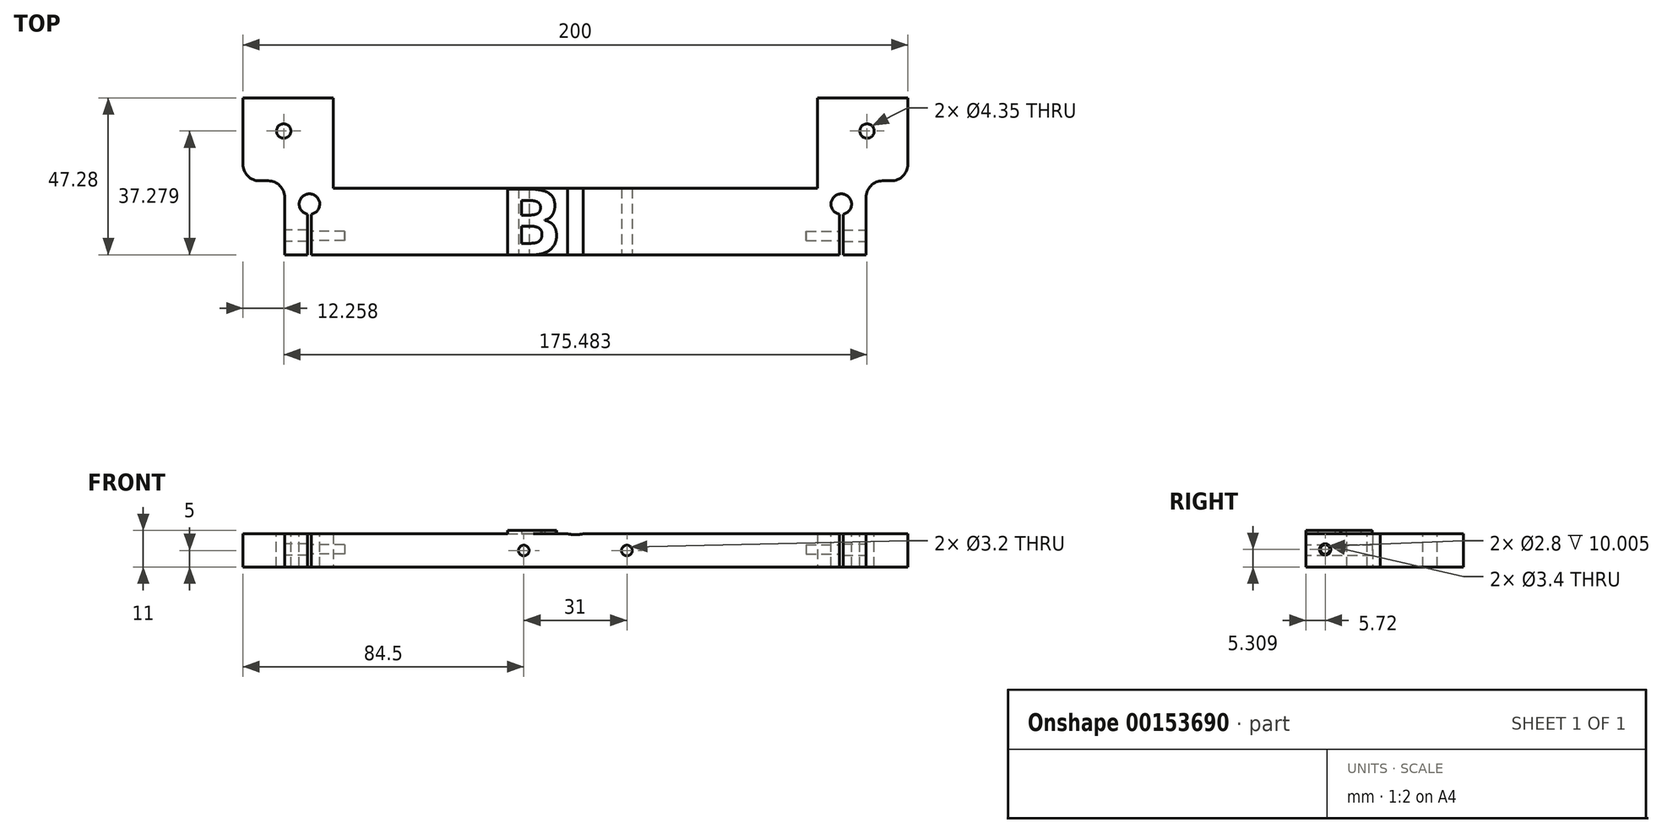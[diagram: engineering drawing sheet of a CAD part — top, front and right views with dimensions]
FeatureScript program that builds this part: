
annotation { "Feature Type Name" : "Feature", "Feature Type Description" : "" }
export const myFeature = defineFeature(function(context is Context, id is Id, definition is map)
    precondition{}
    {
        {
            var Q0;
            Q0=qCreatedBy(makeId("Top.planeOp"),FACE);
            var sketch = newSketch(context, id + "F0", { "sketchPlane" : qUnion([Q0])});
            skLineSegment(sketch, "E0", {"start": v(0, -13.82) * mm, "end": v(-87.44, -13.82) * mm});
            skLineSegment(sketch, "E1", {"start": v(-87.44, -13.82) * mm, "end": v(-87.44, 8.46) * mm});
            skLineSegment(sketch, "E2", {"start": v(-87.44, 8.46) * mm, "end": v(-100, 8.46) * mm});
            skLineSegment(sketch, "E3", {"start": v(-100, 8.46) * mm, "end": v(-100, 33.46) * mm});
            skLineSegment(sketch, "E4", {"start": v(-100, 33.46) * mm, "end": v(-72.87, 33.46) * mm});
            skLineSegment(sketch, "E5", {"start": v(-72.87, 33.46) * mm, "end": v(-72.87, 6.18) * mm});
            skLineSegment(sketch, "E6", {"start": v(-72.87, 6.18) * mm, "end": v(0, 6.18) * mm});
            skLineSegment(sketch, "E7", {"start": v(0, 6.18) * mm, "end": v(0, -13.82) * mm});
            skSolve(sketch);
        }
        {
            var Q0;
            Q0=qSketchRegion(id+"F0",true);
            extrude(context, id + "F1", {"entities" : qUnion([Q0]), "depth" : 10 * mm});
        }
        {
            var Q0;
            Q0=makeQuery(id+"F1.opExtrude","SWEPT_FACE",FACE,{"disambiguationData":[OSD([sQuery(id+"F0.wireOp",EDGE,"E0")])]});
            var sketch = newSketch(context, id + "F2", { "sketchPlane" : qUnion([Q0])});
            skLineSegment(sketch, "E8", {"start": v(0, 5) * mm, "end": v(0, 5) * mm});
            skCircle(sketch, "E9", {"center": v(-15.5, 5) * mm, "radius": 1.6 * mm});
            skCircle(sketch, "E10", {"center": v(0, 20.5) * mm, "radius": 10.75 * mm});
            skSolve(sketch);
        }
        {
            var Q0;
            Q0=qSketchRegion(id+"F2",true);
            extrude(context, id + "F3", {"entities" : qUnion([Q0]), "operationType" : NewBodyOperationType.REMOVE, "endBound" : BoundingType.THROUGH_ALL, "oppositeDirection" : true, "depth" : 25 * mm});
        }
        {
            var Q0;
            {var subQ0=makeQuery(id+"F1.opExtrude","CAP_FACE",FACE,{"disambiguationData":[OSD([sQuery(id+"F0.wireOp",EDGE,"E0"),sQuery(id+"F0.wireOp",EDGE,"fd64a43a-5635-4f94-a977-4dd36923accb"),sQuery(id+"F0.wireOp",EDGE,"1334f7d4-4c90-4769-8fa3-fe5f576fb005"),sQuery(id+"F0.wireOp",EDGE,"E1"),sQuery(id+"F0.wireOp",EDGE,"E2"),sQuery(id+"F0.wireOp",EDGE,"E3"),sQuery(id+"F0.wireOp",EDGE,"E4"),sQuery(id+"F0.wireOp",EDGE,"E5"),sQuery(id+"F0.wireOp",EDGE,"E6"),sQuery(id+"F0.wireOp",EDGE,"E7")])],"isStart":false});Q0=makeQuery(id+"F11.boolean.opBoolean","MERGE",FACE,{"derivedFrom":[subQ0,makeQuery(id+"F11.opPattern","COPY",FACE,{"derivedFrom":subQ0,"instanceName":"1"})]});}
            var sketch = newSketch(context, id + "F4", { "sketchPlane" : qUnion([Q0])});
            skCircle(sketch, "E11", {"center": v(-80, 1.46) * mm, "radius": 3.1 * mm});
            skCircle(sketch, "E12", {"center": v(-87.74, 23.46) * mm, "radius": 2.17 * mm});
            skLineSegment(sketch, "E13", {"start": v(-80, 1.46) * mm, "end": v(-80, -13.82) * mm, "construction": true});
            skLineSegment(sketch, "E14.bottom", {"start": v(-80.55, -0.71) * mm, "end": v(-79.45, -0.71) * mm});
            skLineSegment(sketch, "E14.top", {"start": v(-80.55, -13.82) * mm, "end": v(-79.45, -13.82) * mm});
            skLineSegment(sketch, "E14.left", {"start": v(-80.55, -0.71) * mm, "end": v(-80.55, -13.82) * mm});
            skLineSegment(sketch, "E14.right", {"start": v(-79.45, -0.71) * mm, "end": v(-79.45, -13.82) * mm});
            skPoint(sketch, "E15", {"position": v(-80, -0.71) * mm});
            skSolve(sketch);
        }
        {
            var Q0;
            Q0=qSketchRegion(id+"F4",true);
            var Q1;
            {var subQ3=sQuery(id+"F4.wireOp",EDGE,"E14.bottom");Q1=makeQuery(id+"F4.imprint","IMPRINT",FACE,{"disambiguationData":[TD([[makeQuery(id+"F4.imprint","IMPRINT",EDGE,{"derivedFrom":subQ3}),-1.0]])]});}
            extrude(context, id + "F5", {"entities" : qUnion([Q0, Q1]), "operationType" : NewBodyOperationType.REMOVE, "endBound" : BoundingType.THROUGH_ALL, "oppositeDirection" : true, "depth" : 25 * mm});
        }
        {
            var Q0;
            Q0=makeQuery(id+"F1.opExtrude","SWEPT_EDGE",EDGE,{"disambiguationData":[OSD([sQuery(id+"F0.wireOp",EDGE,"E2"),sQuery(id+"F0.wireOp",EDGE,"E3")])]});
            fillet(context, id + "F6", {"entities" : qUnion([Q0]), "radius" : 5 * mm, "tangentPropagation" : true, "allowEdgeOverflow" : false});
        }
        {
            var Q0;
            Q0=makeQuery(id+"F1.opExtrude","SWEPT_EDGE",EDGE,{"disambiguationData":[OSD([sQuery(id+"F0.wireOp",EDGE,"E1"),sQuery(id+"F0.wireOp",EDGE,"E2")])]});
            fillet(context, id + "F7", {"entities" : qUnion([Q0]), "radius" : 5 * mm, "tangentPropagation" : true, "allowEdgeOverflow" : false});
        }
        {
            var Q0;
            Q0=makeQuery(id+"F1.opExtrude","SWEPT_FACE",FACE,{"disambiguationData":[OSD([sQuery(id+"F0.wireOp",EDGE,"E1")])]});
            var sketch = newSketch(context, id + "F8", { "sketchPlane" : qUnion([Q0])});
            skCircle(sketch, "E16", {"center": v(8.1, 5.3) * mm, "radius": 1.7 * mm});
            skCircle(sketch, "E17", {"center": v(8.1, 5.3) * mm, "radius": 1.4 * mm});
            skSolve(sketch);
        }
        {
            var Q0;
            Q0=makeQuery(id+"F8.imprint","IMPRINT",FACE,{"disambiguationData":[TD([[makeQuery(id+"F8.imprint","IMPRINT",EDGE,{"derivedFrom":sQuery(id+"F8.wireOp",EDGE,"E17")}),1.0]])]});
            extrude(context, id + "F9", {"entities" : qUnion([Q0]), "operationType" : NewBodyOperationType.REMOVE, "oppositeDirection" : true, "depth" : 18 * mm});
        }
        {
            var Q0;
            Q0=makeQuery(id+"F8.imprint","IMPRINT",FACE,{"disambiguationData":[TD([[makeQuery(id+"F8.imprint","IMPRINT",EDGE,{"derivedFrom":sQuery(id+"F8.wireOp",EDGE,"E17")}),1.0]])]});
            var Q1;
            Q1=makeQuery(id+"F8.imprint","IMPRINT",FACE,{"disambiguationData":[TD([[makeQuery(id+"F8.imprint","IMPRINT",EDGE,{"derivedFrom":sQuery(id+"F8.wireOp",EDGE,"E16")}),1.0]])]});
            extrude(context, id + "F10", {"entities" : qUnion([Q0, Q1]), "operationType" : NewBodyOperationType.REMOVE, "endBound" : BoundingType.UP_TO_NEXT, "oppositeDirection" : true, "depth" : 25 * mm});
        }
        {
            var Q0;
            Q0=makeQuery(id+"F1.opExtrude","SWEPT_BODY",BODY,{"disambiguationData":[OSD([sQuery(id+"F0.wireOp",EDGE,"E0"),sQuery(id+"F0.wireOp",EDGE,"fd64a43a-5635-4f94-a977-4dd36923accb"),sQuery(id+"F0.wireOp",EDGE,"1334f7d4-4c90-4769-8fa3-fe5f576fb005"),sQuery(id+"F0.wireOp",EDGE,"E1"),sQuery(id+"F0.wireOp",EDGE,"E2"),sQuery(id+"F0.wireOp",EDGE,"E3"),sQuery(id+"F0.wireOp",EDGE,"E4"),sQuery(id+"F0.wireOp",EDGE,"E5"),sQuery(id+"F0.wireOp",EDGE,"E6"),sQuery(id+"F0.wireOp",EDGE,"E7")])]});
            var Q1;
            Q1=qCreatedBy(makeId("Right.planeOp"),FACE);
            mirror(context, id + "F11", {"operationType" : NewBodyOperationType.ADD, "entities" : qUnion([Q0]), "mirrorPlane" : qUnion([Q1])});
        }
        {
            var Q0;
            Q0=makeQuery(id+"F1.opExtrude","CAP_FACE",FACE,{"disambiguationData":[OSD([sQuery(id+"F0.wireOp",EDGE,"E0"),sQuery(id+"F0.wireOp",EDGE,"E1"),sQuery(id+"F0.wireOp",EDGE,"E2"),sQuery(id+"F0.wireOp",EDGE,"E3"),sQuery(id+"F0.wireOp",EDGE,"E4"),sQuery(id+"F0.wireOp",EDGE,"E5"),sQuery(id+"F0.wireOp",EDGE,"E6"),sQuery(id+"F0.wireOp",EDGE,"E7")])],"isStart":false});
            var sketch = newSketch(context, id + "F12", { "sketchPlane" : qUnion([Q0])});
            skText(sketch, "E18", { "text": "B", "fontName": "OpenSans-Bold.ttf"});
            const initialGuessF12  = {"E18": [-0.02287, -0.01382, 1, 0, 0.02]};
            skSetInitialGuess(sketch, initialGuessF12);
            skSolve(sketch);
        }
        {
            var Q0;
            Q0=qSketchRegion(id+"F12",true);
            extrude(context, id + "F13", {"entities" : qUnion([Q0]), "operationType" : NewBodyOperationType.ADD, "depth" : 1 * mm});
        }
        {
            var Q0;
            {var subQ0=makeQuery(id+"F1.opExtrude","CAP_FACE",FACE,{"disambiguationData":[OSD([sQuery(id+"F0.wireOp",EDGE,"E0"),sQuery(id+"F0.wireOp",EDGE,"E1"),sQuery(id+"F0.wireOp",EDGE,"E2"),sQuery(id+"F0.wireOp",EDGE,"E3"),sQuery(id+"F0.wireOp",EDGE,"E4"),sQuery(id+"F0.wireOp",EDGE,"E5"),sQuery(id+"F0.wireOp",EDGE,"E6"),sQuery(id+"F0.wireOp",EDGE,"E7")])],"isStart":true});Q0=makeQuery(id+"F11.boolean.opBoolean","MERGE",FACE,{"derivedFrom":[subQ0,makeQuery(id+"F11.opPattern","COPY",FACE,{"derivedFrom":subQ0,"instanceName":"1"})]});}
            var sketch = newSketch(context, id + "F14", { "sketchPlane" : qUnion([Q0])});
            skLineSegment(sketch, "E19", {"start": v(-86.43, -28.46) * mm, "end": v(86.43, -28.46) * mm});
            skPoint(sketch, "E19.startSnap0", {"position": v(-86.43, -33.46) * mm});
            skPoint(sketch, "E19.endSnap0", {"position": v(86.43, -33.46) * mm});
            skSolve(sketch);
        }
    });
